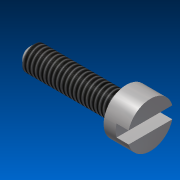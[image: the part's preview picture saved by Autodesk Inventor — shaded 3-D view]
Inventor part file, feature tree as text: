
AUTODESK INVENTOR PART (.ipt)
format: ipt  version: 2015 SP1 (Build 190203100, 203)  size: 109,056 bytes
history: native  units: mm
features: extrude x3, sketch x1, chamfer x1, thread x1, projected_geometry x1
ambient origin geometry x8: Origin, YZ Plane, XZ Plane, XY Plane, X Axis, Y Axis, Z Axis, Center Point
bodies: Solid1 (feature_tree)
feature tree (7):
  sketch  "Sketch1"  dims[d0=4.0mm d1=7.5mm d2=16.0mm d3=0.0mm d4=4.0mm d5=0.0mm d6=2.0mm d7=0.0mm d10=0.8mm d11=2.0mm d12=45.0deg d13=5.0mm d14=0.0mm d15=2.0mm]
  extrude  "Extrusion1"  Depth=2.0mm
  extrude  "Extrusion2"  Depth=16.0mm TaperAngle=0.0deg
  extrude  "Extrusion3"  Depth=4.0mm TaperAngle=0.0deg
  chamfer  "Chamfer1"  Distance=2.0mm
  thread  "Thread2"  [1 undecoded]
  projected_geometry  "Projected Loop1"
note: 1 required parameter value undecoded (feature->parameter linkage not recoverable at this tier; creation-order binding heuristic only, values carry confidence <= 0.55)
